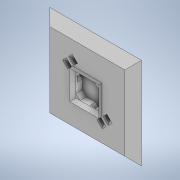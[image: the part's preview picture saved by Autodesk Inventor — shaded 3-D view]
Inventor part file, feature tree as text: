
AUTODESK INVENTOR PART (.ipt)
format: ipt  version: 2021 (Build 250183000, 183)  size: 207,872 bytes
history: native  units: in
note: dims shown in document units (in); Inventor stores cm internally (conversion verified against a paired STEP export)
features: sketch x5, extrude x3, plane x3, chamfer x2, projected_geometry x2, sweep x1, mirror x1
ambient origin geometry x8: Origin, YZ Plane, XZ Plane, XY Plane, X Axis, Y Axis, Z Axis, Center Point
bodies: Solid1 (feature_tree)
feature tree (17):
  extrude  "Extrusion1"  Depth=0.1575in
  chamfer  "Chamfer1"  Distance=0.1575in
  extrude  "Extrusion2"  Depth=0.1181in TaperAngle=0.0deg
  plane  "Work Plane3"
  plane  "Work Plane4"
  plane  "Work Plane5"
  sweep  "Sweep3"
  mirror  "Mirror2"
  extrude  "Extrusion7"  Depth=0.0984in
  chamfer  "Chamfer6"  Distance=0.0492in
  sketch  "Sketch1"  dims[d0=1.7323in d1=1.7323in d2=0.1575in d3=0.0in]
  sketch  "Sketch2"  dims[d4=0.1575in d5=0.0787in d6=45.0deg d8=0.1181in d9=0.0in]
  projected_geometry  "Projected Loop1"
  sketch  "Sketch13"  dims[d86=0.0787in d87=0.0787in]
  sketch  "Sketch14"  dims[d88=0.0492in d89=0.0984in]
  sketch  "Sketch15"  dims[d90=0.0984in d91=0.0492in d92=0.3937in d93=45.0deg d94=0.3937in d95=0.0in d96=0.0in d97=0.0591in d98=0.0591in d99=0.0in d100=0.0591in d101=0.0787in d102=45.0deg]
  projected_geometry  "Projected Loop6"
